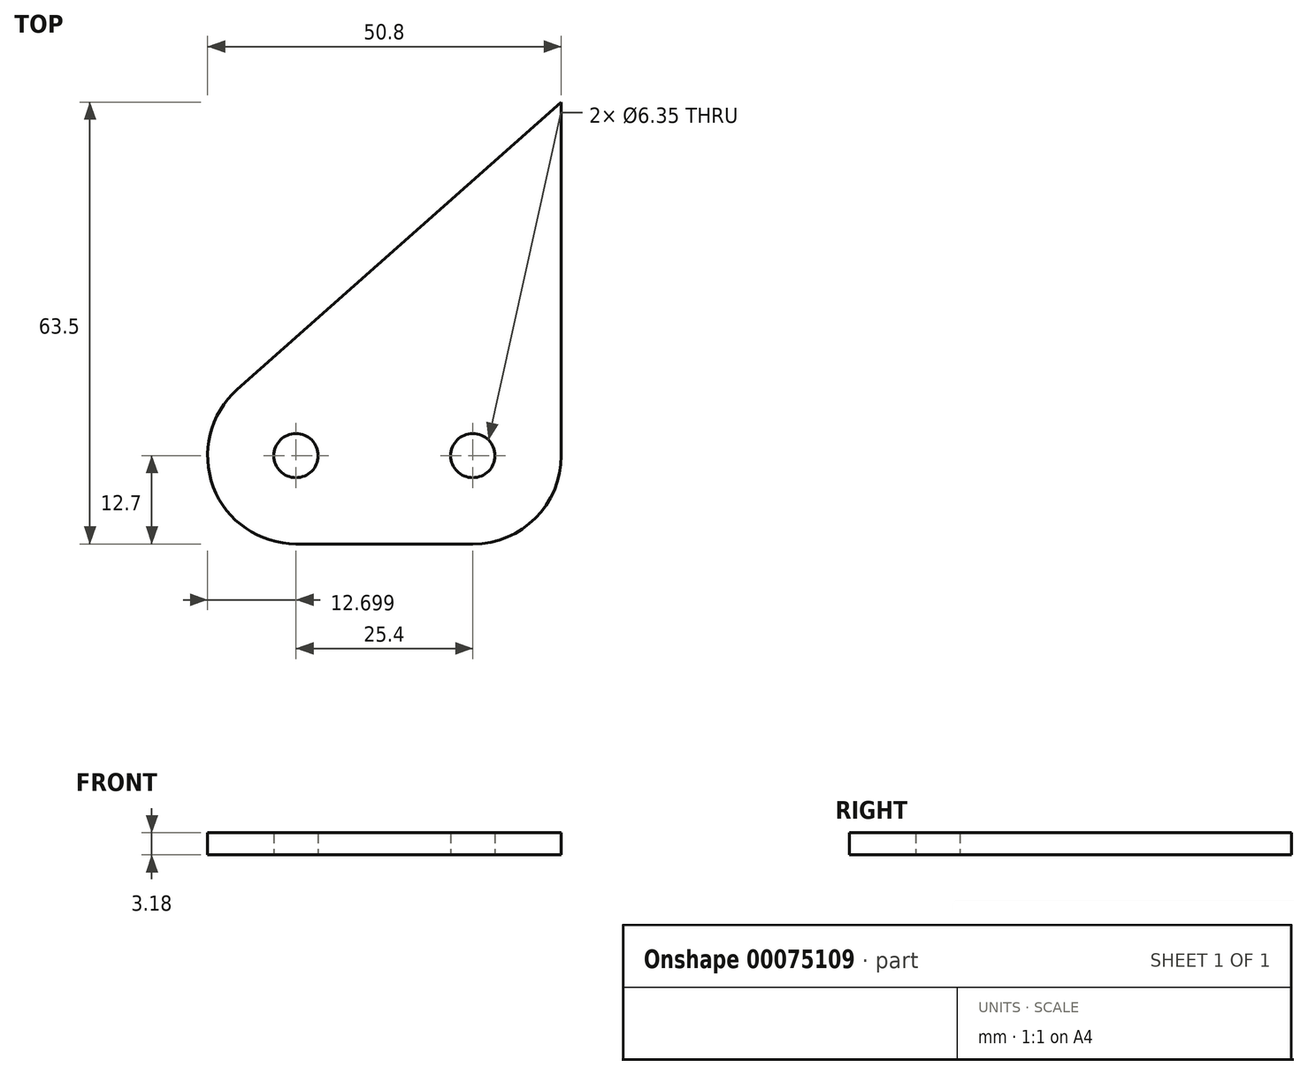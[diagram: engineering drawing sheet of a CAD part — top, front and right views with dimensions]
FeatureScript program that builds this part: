
annotation { "Feature Type Name" : "Feature", "Feature Type Description" : "" }
export const myFeature = defineFeature(function(context is Context, id is Id, definition is map)
    precondition{}
    {
        {
            var Q0;
            Q0=qCreatedBy(makeId("Top.planeOp"),FACE);
            var sketch = newSketch(context, id + "F0", { "sketchPlane" : qUnion([Q0])});
            skLineSegment(sketch, "E0", {"start": v(-1.12, -12.7) * mm, "end": v(24.28, -12.7) * mm});
            skLineSegment(sketch, "E1", {"start": v(36.98, 0) * mm, "end": v(36.98, 50.8) * mm});
            skLineSegment(sketch, "E2", {"start": v(-9.55, 9.5) * mm, "end": v(36.98, 50.8) * mm});
            skArc(sketch, "E3", {"start": v(24.28, -12.7) * mm, "mid": v(33.26, -8.98) * mm, "end": v(36.98, 0) * mm});
            skArc(sketch, "E4", {"start": v(-9.55, 9.5) * mm, "mid": v(-13, -4.5) * mm, "end": v(-1.12, -12.7) * mm});
            skSolve(sketch);
        }
        {
            var Q0;
            Q0=makeQuery(id+"F0.imprint","IMPRINT",FACE,{"disambiguationData":[TD([[makeQuery(id+"F0.imprint","IMPRINT",EDGE,{"derivedFrom":sQuery(id+"F0.wireOp",EDGE,"E0")}),1.0]])]});
            extrude(context, id + "F1", {"entities" : qUnion([Q0]), "depth" : 3.17 * mm});
        }
        {
            var Q0;
            Q0=makeQuery(id+"F1.opExtrude","CAP_FACE",FACE,{"disambiguationData":[OSD([sQuery(id+"F0.wireOp",EDGE,"E0"),sQuery(id+"F0.wireOp",EDGE,"E1"),sQuery(id+"F0.wireOp",EDGE,"E2"),sQuery(id+"F0.wireOp",EDGE,"E3"),sQuery(id+"F0.wireOp",EDGE,"E4")])],"isStart":false});
            var sketch = newSketch(context, id + "F2", { "sketchPlane" : qUnion([Q0])});
            skPoint(sketch, "E5", {"position": v(-1.12, 0) * mm});
            skPoint(sketch, "E6", {"position": v(24.28, 0) * mm});
            skSolve(sketch);
        }
        {
            var Q0;
            Q0=sQuery(id+"F2.wireOp",VERTEX,"E6");
            var Q1;
            Q1=sQuery(id+"F2.wireOp",VERTEX,"E5");
            var Q2;
            Q2=makeQuery(id+"F1.opExtrude","SWEPT_BODY",BODY,{"disambiguationData":[OSD([sQuery(id+"F0.wireOp",EDGE,"E0"),sQuery(id+"F0.wireOp",EDGE,"E1"),sQuery(id+"F0.wireOp",EDGE,"E2"),sQuery(id+"F0.wireOp",EDGE,"E3"),sQuery(id+"F0.wireOp",EDGE,"E4")])]});
            hole(context, id + "F3", {"style" : HoleStyle.SIMPLE, "holeDiameter" : 6.35 * mm, "endStyle" : HoleEndStyle.THROUGH, "locations" : qUnion([Q0, Q1]), "scope" : qUnion([Q2])});
        }
    });
